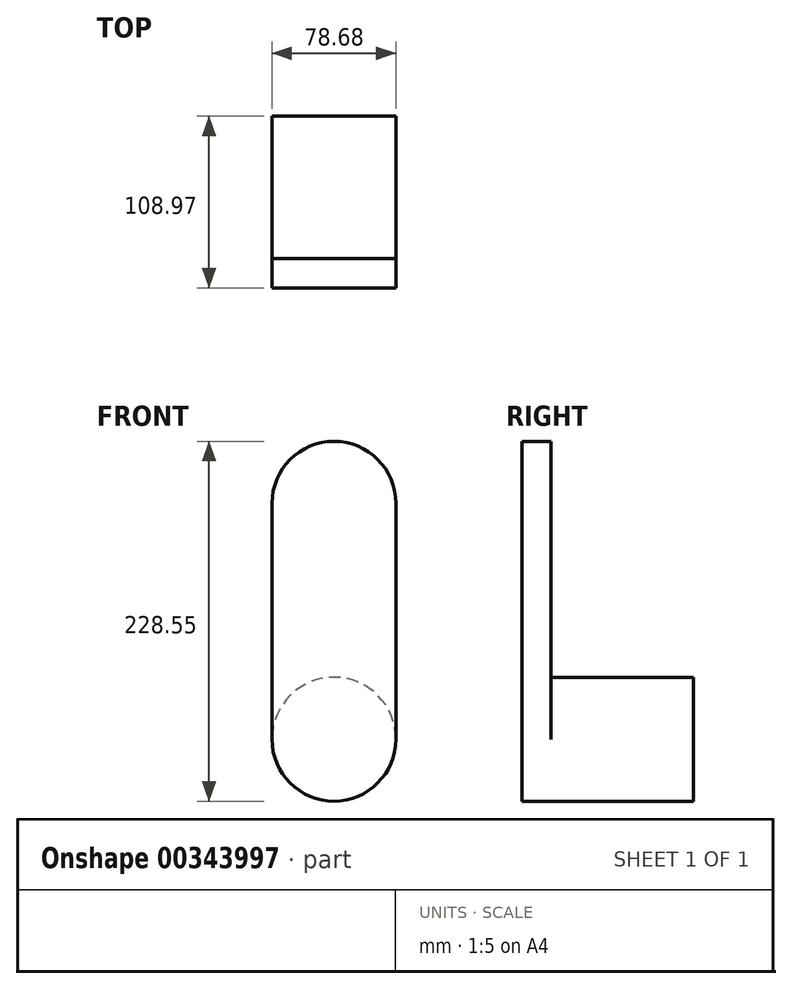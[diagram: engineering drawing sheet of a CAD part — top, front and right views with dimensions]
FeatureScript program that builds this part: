
annotation { "Feature Type Name" : "Feature", "Feature Type Description" : "" }
export const myFeature = defineFeature(function(context is Context, id is Id, definition is map)
    precondition{}
    {
        {
            var Q0;
            Q0=qCreatedBy(makeId("Front.planeOp"),FACE);
            var sketch = newSketch(context, id + "F0", { "sketchPlane" : qUnion([Q0])});
            skLineSegment(sketch, "E0.bottom", {"start": v(39.34, 72.27) * mm, "end": v(-39.34, 72.27) * mm});
            skLineSegment(sketch, "E0.top", {"start": v(39.34, -77.6) * mm, "end": v(-39.34, -77.6) * mm});
            skLineSegment(sketch, "E0.left", {"start": v(39.34, 72.27) * mm, "end": v(39.34, -77.6) * mm});
            skLineSegment(sketch, "E0.right", {"start": v(-39.34, 72.27) * mm, "end": v(-39.34, -77.6) * mm});
            skPoint(sketch, "E0.middle", {"position": v(0, -2.66) * mm});
            skCircle(sketch, "E1", {"center": v(0, 72.27) * mm, "radius": 39.34 * mm});
            skCircle(sketch, "E2", {"center": v(0, -77.6) * mm, "radius": 39.34 * mm});
            skSolve(sketch);
        }
        {
            var Q0;
            {var subQ0=sQuery(id+"F0.wireOp",EDGE,"E0.top");Q0=makeQuery(id+"F0.imprint","IMPRINT",FACE,{"disambiguationData":[TD([[makeQuery(id+"F0.imprint","IMPRINT",EDGE,{"derivedFrom":subQ0}),1.0]])]});}
            var Q1;
            {var subQ0=sQuery(id+"F0.wireOp",EDGE,"E0.top");Q1=makeQuery(id+"F0.imprint","IMPRINT",FACE,{"disambiguationData":[TD([[makeQuery(id+"F0.imprint","IMPRINT",EDGE,{"derivedFrom":subQ0}),-1.0]])]});}
            extrude(context, id + "F1", {"entities" : qUnion([Q0, Q1]), "oppositeDirection" : true, "depth" : 108.97 * mm});
        }
        {
            var Q0;
            {var subQ0=sQuery(id+"F0.wireOp",EDGE,"E0.left");Q0=makeQuery(id+"F0.imprint","IMPRINT",FACE,{"disambiguationData":[TD([[makeQuery(id+"F0.imprint","IMPRINT",EDGE,{"derivedFrom":subQ0}),-1.0]])]});}
            var Q1;
            {var subQ0=sQuery(id+"F0.wireOp",EDGE,"E0.bottom");Q1=makeQuery(id+"F0.imprint","IMPRINT",FACE,{"disambiguationData":[TD([[makeQuery(id+"F0.imprint","IMPRINT",EDGE,{"derivedFrom":subQ0}),1.0]])]});}
            var Q2;
            {var subQ0=sQuery(id+"F0.wireOp",EDGE,"E0.bottom");Q2=makeQuery(id+"F0.imprint","IMPRINT",FACE,{"disambiguationData":[TD([[makeQuery(id+"F0.imprint","IMPRINT",EDGE,{"derivedFrom":subQ0}),-1.0]])]});}
            extrude(context, id + "F2", {"entities" : qUnion([Q0, Q1, Q2]), "operationType" : NewBodyOperationType.ADD, "oppositeDirection" : true, "depth" : 18.54 * mm});
        }
    });
